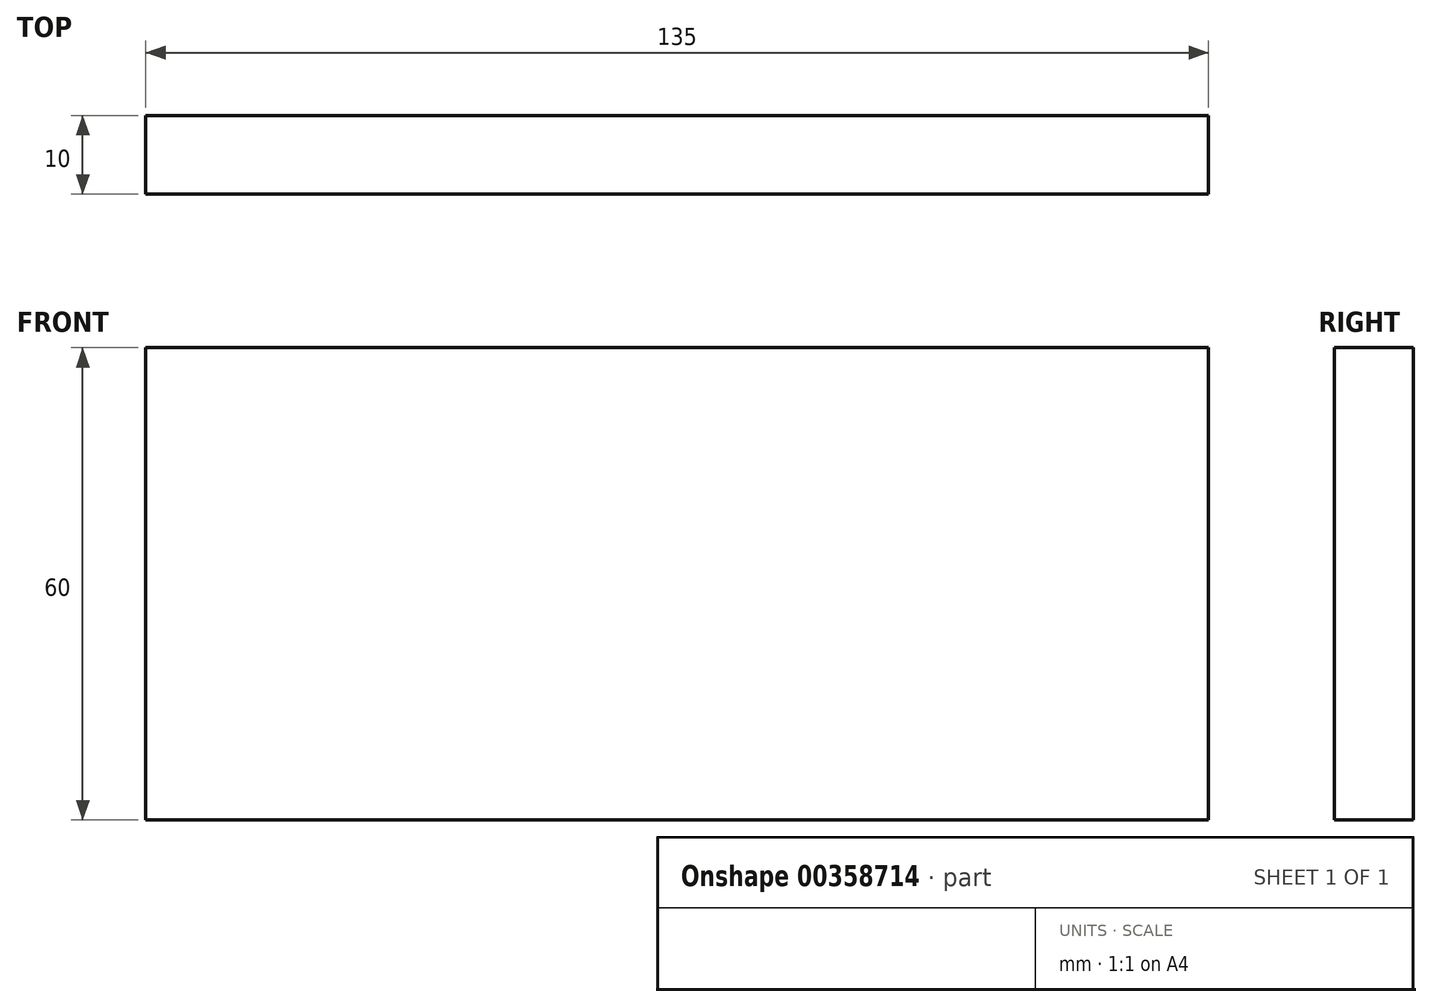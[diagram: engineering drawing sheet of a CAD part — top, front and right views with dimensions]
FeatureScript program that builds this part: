
annotation { "Feature Type Name" : "Feature", "Feature Type Description" : "" }
export const myFeature = defineFeature(function(context is Context, id is Id, definition is map)
    precondition{}
    {
        {
            var Q0;
            Q0=qCreatedBy(makeId("Right.planeOp"),FACE);
            var sketch = newSketch(context, id + "F0", { "sketchPlane" : qUnion([Q0])});
            skLineSegment(sketch, "E0.bottom", {"start": v(5, -30) * mm, "end": v(-5, -30) * mm});
            skLineSegment(sketch, "E0.top", {"start": v(5, 30) * mm, "end": v(-5, 30) * mm});
            skLineSegment(sketch, "E0.left", {"start": v(5, -30) * mm, "end": v(5, 30) * mm});
            skLineSegment(sketch, "E0.right", {"start": v(-5, -30) * mm, "end": v(-5, 30) * mm});
            skPoint(sketch, "E0.middle", {"position": v(0, 0) * mm});
            skSolve(sketch);
        }
        {
            var Q0;
            Q0 = qSketchRegion(id + "F0", true);
            extrude(context, id + "F1", {"entities" : qUnion([Q0]), "endBound" : BoundingType.SYMMETRIC, "depth" : 135 * mm});
        }
    });
